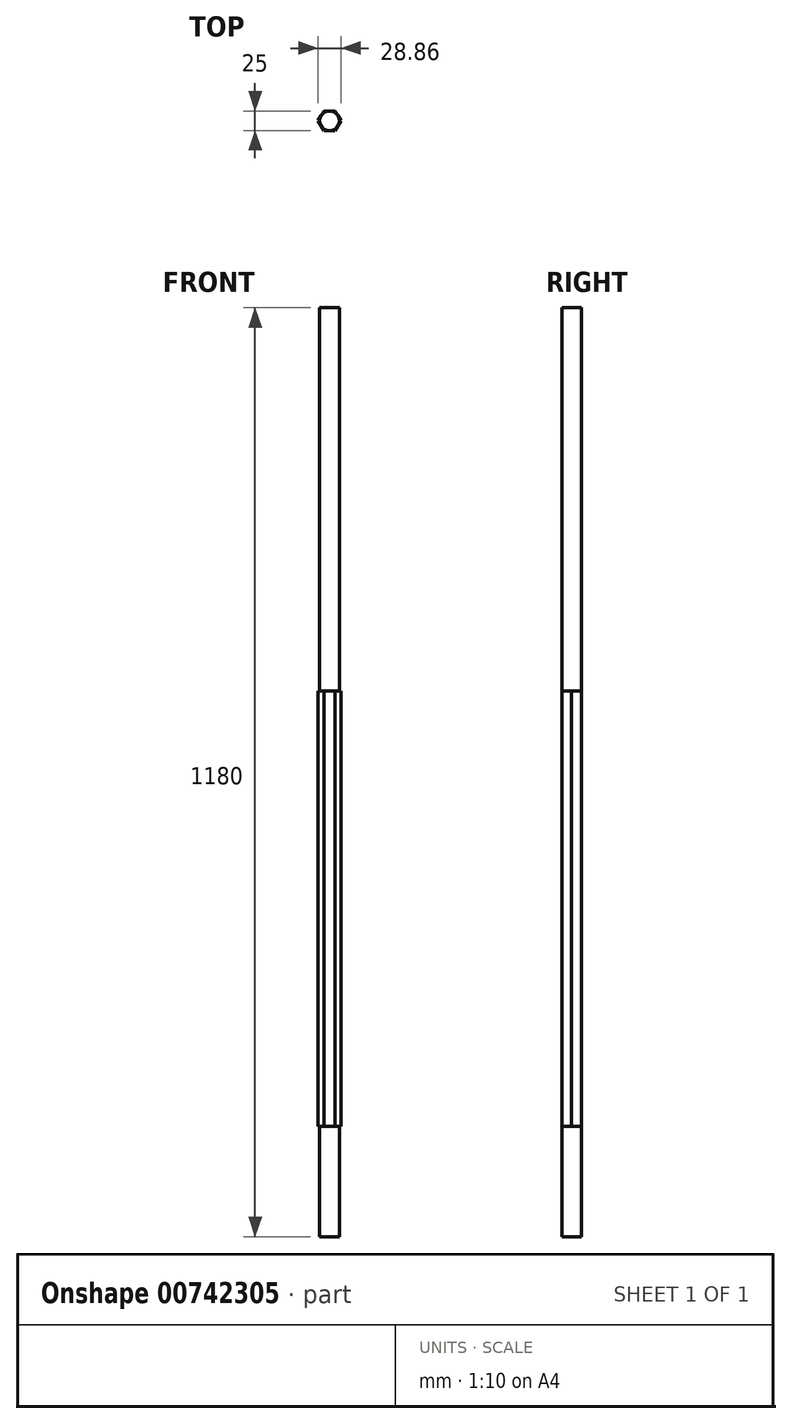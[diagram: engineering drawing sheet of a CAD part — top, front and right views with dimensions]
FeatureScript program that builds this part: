
annotation { "Feature Type Name" : "Feature", "Feature Type Description" : "" }
export const myFeature = defineFeature(function(context is Context, id is Id, definition is map)
    precondition{}
    {
        {
            var Q0;
            Q0=qCreatedBy(makeId("Top.planeOp"),FACE);
            var sketch = newSketch(context, id + "F0", { "sketchPlane" : qUnion([Q0])});
            skCircle(sketch, "E0", {"center": v(0, 0) * mm, "radius": 12.5 * mm});
            skSolve(sketch);
        }
        {
            var Q0;
            Q0 = qSketchRegion(id + "F0", true);
            extrude(context, id + "F1", {"entities" : qUnion([Q0]), "depth" : 140 * mm, "offsetDistance" : 25 * mm});
        }
        {
            var Q0;
            Q0=makeQuery(id+"F1.opExtrude","CAP_FACE",FACE,{"disambiguationData":[OSD([sQuery(id+"F0.wireOp",EDGE,"E0")])],"isStart":false});
            var sketch = newSketch(context, id + "F2", { "sketchPlane" : qUnion([Q0])});
            skCircle(sketch, "E1.cCircle", {"center": v(0, 0) * mm, "radius": 12.5 * mm, "construction": true});
            skLineSegment(sketch, "E1.0", {"start": v(-7.22, 12.5) * mm, "end": v(7.22, 12.5) * mm});
            skLineSegment(sketch, "E1.1", {"start": v(7.22, 12.5) * mm, "end": v(14.43, 0) * mm});
            skLineSegment(sketch, "E1.2", {"start": v(14.43, 0) * mm, "end": v(7.22, -12.5) * mm});
            skLineSegment(sketch, "E1.3", {"start": v(7.22, -12.5) * mm, "end": v(-7.22, -12.5) * mm});
            skLineSegment(sketch, "E1.4", {"start": v(-7.22, -12.5) * mm, "end": v(-14.43, 0) * mm});
            skLineSegment(sketch, "E1.5", {"start": v(-14.43, 0) * mm, "end": v(-7.22, 12.5) * mm});
            skPoint(sketch, "E1.0.midPoint", {"position": v(0, 12.5) * mm});
            skSolve(sketch);
        }
        {
            var Q0;
            Q0 = qSketchRegion(id + "F2", true);
            extrude(context, id + "F3", {"entities" : qUnion([Q0]), "operationType" : NewBodyOperationType.ADD, "depth" : 553 * mm, "offsetDistance" : 25 * mm});
        }
        {
            var Q0;
            Q0=makeQuery(id+"F3.opExtrude","CAP_FACE",FACE,{"disambiguationData":[OSD([sQuery(id+"F2.wireOp",EDGE,"E1.0"),sQuery(id+"F2.wireOp",EDGE,"E1.1"),sQuery(id+"F2.wireOp",EDGE,"E1.2"),sQuery(id+"F2.wireOp",EDGE,"E1.3"),sQuery(id+"F2.wireOp",EDGE,"E1.4"),sQuery(id+"F2.wireOp",EDGE,"E1.5")])],"isStart":false});
            var sketch = newSketch(context, id + "F4", { "sketchPlane" : qUnion([Q0])});
            skCircle(sketch, "E2", {"center": v(0, 0) * mm, "radius": 12.5 * mm});
            skSolve(sketch);
        }
        {
            var Q0;
            Q0 = qSketchRegion(id + "F4", true);
            extrude(context, id + "F5", {"entities" : qUnion([Q0]), "operationType" : NewBodyOperationType.ADD, "depth" : 487 * mm, "offsetDistance" : 25 * mm});
        }
    });
